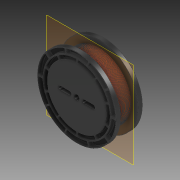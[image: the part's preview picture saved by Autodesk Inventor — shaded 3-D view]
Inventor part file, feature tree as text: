
AUTODESK INVENTOR PART (.ipt)
format: ipt  version: 2020 (Build 240168000, 168)  size: 2,467,840 bytes
history: native  units: mm
features: sketch x7, extrude x6, fillet x4, pattern_circular x3, projected_geometry x2, revolve x1, plane x1
ambient origin geometry x8: Origin, YZ Plane, XZ Plane, XY Plane, X Axis, Y Axis, Z Axis, Center Point
bodies: Solid1 (feature_tree), Solid2 (feature_tree), Solid3 (feature_tree), Solid4 (feature_tree)
feature tree (24):
  extrude  "Extrusion1"  Depth=35.0mm TaperAngle=0.0deg
  extrude  "Extrusion2"  Depth=134.0mm TaperAngle=0.0deg
  extrude  "Extrusion3"  Depth=35.0mm TaperAngle=0.0deg
  sketch  "Sketch5"  dims[d6=606.0mm d7=35.0mm d8=0.0mm]
  extrude  "Extrusion5"  Depth=30.0mm
  fillet  "Fillet1"  Radius=40.0mm
  pattern_circular  "Circular Pattern1"  Count=3  [1 undecoded]
  sketch  "Sketch6"  dims[d12=40.0mm d13=40.0mm d14=40.0mm d15=30.0mm]
  extrude  "Extrusion6"  Depth=15.0mm
  fillet  "Fillet3"  Radius=15.0mm
  pattern_circular  "Circular Pattern2"  Count=25  [1 undecoded]
  fillet  "Fillet4"  Radius=125.0mm
  sketch  "Sketch7"  dims[d16=30.0mm d17=15.0mm d18=15.0mm]
  extrude  "Extrusion7"  Depth=10.0mm
  fillet  "Fillet5"  Radius=12.566371mm
  pattern_circular  "Circular Pattern3"  [2 undecoded]
  revolve  "Revolution1"  [1 undecoded]
  plane  "Work Plane2"
  sketch  "Sketch2"  dims[d0=606.0mm d1=35.0mm d2=0.0mm]
  sketch  "Sketch3"  dims[d3=486.0mm d4=134.0mm d5=0.0mm]
  projected_geometry  "Projected Loop1"
  projected_geometry  "Projected Loop2"
  sketch  "Sketch8"  dims[d19=115.0mm]
  sketch  "Sketch9"  dims[d20=57.5mm d21=250.0mm d22=125.0mm d24=18.849556mm d25=12.566371mm d26=45.0mm d27=5.0mm d28=30.0mm d29=0.0mm d30=2.0mm d31=100.0mm d32=360.0deg d34=30.0mm d35=5.0mm d36=30.0mm d37=0.0mm d39=2.0mm d40=2.0mm d41=100.0mm d42=360.0deg d44=2.0mm d45=30.0mm d46=0.0mm d47=2.0mm d48=100.0mm d49=360.0deg d51=6.0mm d52=6.0mm d53=0.5mm d54=220.0mm d56=6.09mm d57=10.0mm d59=10.0mm d61=90.0deg]
note: 5 required parameter values undecoded (feature->parameter linkage not recoverable at this tier; creation-order binding heuristic only, values carry confidence <= 0.55)